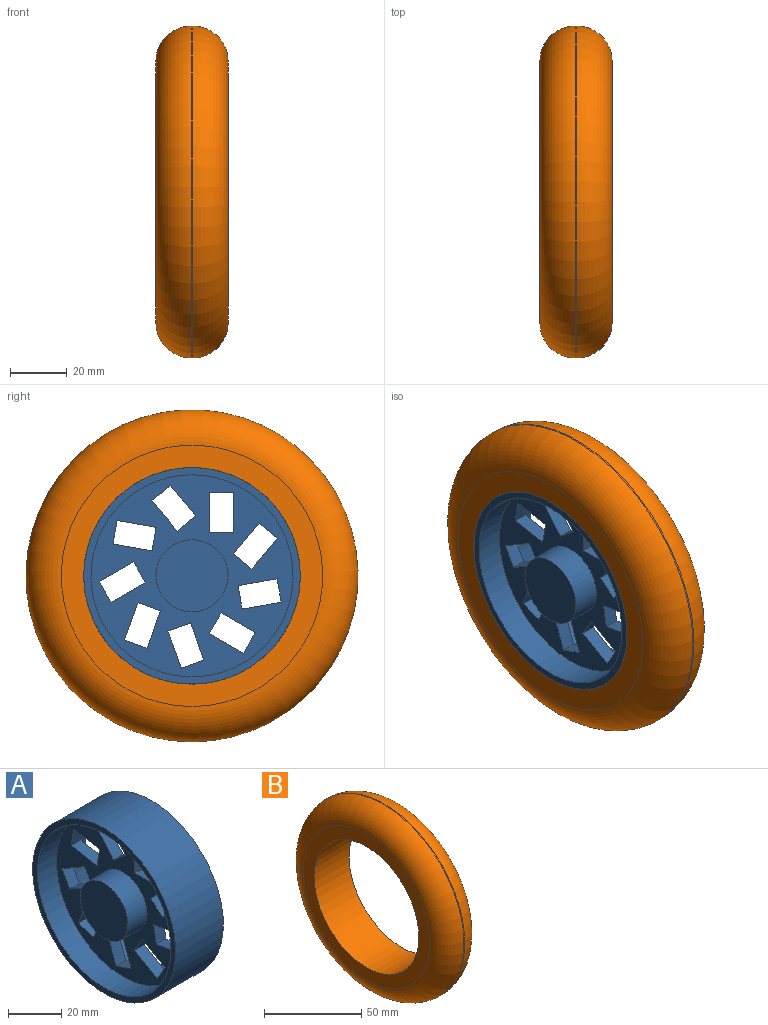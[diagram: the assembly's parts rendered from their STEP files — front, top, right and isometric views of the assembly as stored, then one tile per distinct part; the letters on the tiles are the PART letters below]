
ASSEMBLY  parts=2 mates=1
PART A: 47 faces, bbox 25.4x76.2x76.2 mm
  f0: plane 71.12x71.12mm, normal (1,0,0), area 2410.9mm2, adj f8,f9,f11,f12,f13,f14,f15,f16
  f1: plane 25.4x25.4mm, normal (-1,0,0), area 506.7mm2, adj f2
  f2: cylinder r=12.7mm len=25.4mm, axis (-1,0,0), area 810.7mm2, adj f1,f3
  f3: plane 71.12x71.12mm, normal (-1,0,0), area 2410.9mm2, adj f2,f4,f11,f12,f13,f14,f15,f16
  f4: cylinder r=35.56mm len=71.12mm, axis (-1,0,0), area 2270mm2, adj f3,f5
  f5: plane 76.2x76.2mm, normal (-1,0,0), area 587.8mm2, adj f4,f6
  f6: cylinder r=38.1mm len=76.2mm, axis (-1,0,0), area 6080.5mm2, adj f5,f7
  f7: plane 76.2x76.2mm, normal (1,0,0), area 587.8mm2, adj f6,f8
  f8: cylinder r=35.56mm len=71.12mm, axis (-1,0,0), area 2270mm2, adj f0,f7
  f9: cylinder r=12.7mm len=25.4mm, axis (-1,0,0), area 810.7mm2, adj f0,f10
  f10: plane 25.4x25.4mm, normal (1,0,0), area 506.7mm2, adj f9
  f11: plane 13.94x5.08mm, normal (0,-1,0), area 70.8mm2, adj f0,f3,f12,f14
  f12: plane 8.41x5.08mm, normal (0,0,-1), area 42.7mm2, adj f0,f3,f11,f13
  f13: plane 13.94x5.08mm, normal (0,1,0), area 70.8mm2, adj f0,f3,f12,f14
  f14: plane 8.41x5.08mm, normal (0,0,1), area 42.7mm2, adj f0,f3,f11,f13
  f15: plane 10.68x8.96mm, normal (0,-0.77,0.64), area 70.8mm2, adj f0,f3,f16,f18
  f16: plane 6.44x5.41mm, normal (0,-0.64,-0.77), area 42.7mm2, adj f0,f3,f15,f17
  f17: plane 10.68x8.96mm, normal (0,0.77,-0.64), area 70.8mm2, adj f0,f3,f16,f18
  f18: plane 6.44x5.41mm, normal (0,0.64,0.77), area 42.7mm2, adj f0,f3,f15,f17
  f19: plane 13.72x5.08mm, normal (0,-0.17,0.98), area 70.8mm2, adj f0,f3,f20,f22
  f20: plane 8.28x5.08mm, normal (0,-0.98,-0.17), area 42.7mm2, adj f0,f3,f19,f21
  f21: plane 13.72x5.08mm, normal (0,0.17,-0.98), area 70.8mm2, adj f0,f3,f20,f22
  f22: plane 8.28x5.08mm, normal (0,0.98,0.17), area 42.7mm2, adj f0,f3,f19,f21
  f23: plane 12.07x6.97mm, normal (0,0.5,0.87), area 70.8mm2, adj f0,f3,f24,f26
  f24: plane 7.28x5.08mm, normal (0,-0.87,0.5), area 42.7mm2, adj f0,f3,f23,f25
  f25: plane 12.07x6.97mm, normal (0,-0.5,-0.87), area 70.8mm2, adj f0,f3,f24,f26
  f26: plane 7.28x5.08mm, normal (0,0.87,-0.5), area 42.7mm2, adj f0,f3,f23,f25
  f27: plane 13.1x5.08mm, normal (0,0.94,0.34), area 70.8mm2, adj f0,f3,f28,f30
  f28: plane 7.9x5.08mm, normal (0,-0.34,0.94), area 42.7mm2, adj f0,f3,f27,f29
  f29: plane 13.1x5.08mm, normal (0,-0.94,-0.34), area 70.8mm2, adj f0,f3,f28,f30
  f30: plane 7.9x5.08mm, normal (0,0.34,-0.94), area 42.7mm2, adj f0,f3,f27,f29
  f31: plane 13.1x5.08mm, normal (0,0.94,-0.34), area 70.8mm2, adj f0,f3,f32,f34
  f32: plane 7.9x5.08mm, normal (0,0.34,0.94), area 42.7mm2, adj f0,f3,f31,f33
  f33: plane 13.1x5.08mm, normal (0,-0.94,0.34), area 70.8mm2, adj f0,f3,f32,f34
  f34: plane 7.9x5.08mm, normal (0,-0.34,-0.94), area 42.7mm2, adj f0,f3,f31,f33
  f35: plane 12.07x6.97mm, normal (0,0.5,-0.87), area 70.8mm2, adj f0,f3,f36,f38
  f36: plane 7.28x5.08mm, normal (0,0.87,0.5), area 42.7mm2, adj f0,f3,f35,f37
  f37: plane 12.07x6.97mm, normal (0,-0.5,0.87), area 70.8mm2, adj f0,f3,f36,f38
  f38: plane 7.28x5.08mm, normal (0,-0.87,-0.5), area 42.7mm2, adj f0,f3,f35,f37
  f39: plane 13.72x5.08mm, normal (0,-0.17,-0.98), area 70.8mm2, adj f0,f3,f40,f42
  f40: plane 8.28x5.08mm, normal (0,0.98,-0.17), area 42.7mm2, adj f0,f3,f39,f41
  f41: plane 13.72x5.08mm, normal (0,0.17,0.98), area 70.8mm2, adj f0,f3,f40,f42
  f42: plane 8.28x5.08mm, normal (0,-0.98,0.17), area 42.7mm2, adj f0,f3,f39,f41
  f43: plane 10.68x8.96mm, normal (0,-0.77,-0.64), area 70.8mm2, adj f0,f3,f44,f46
  f44: plane 6.44x5.41mm, normal (0,0.64,-0.77), area 42.7mm2, adj f0,f3,f43,f45
  f45: plane 10.68x8.96mm, normal (0,0.77,0.64), area 70.8mm2, adj f0,f3,f44,f46
  f46: plane 6.44x5.41mm, normal (0,-0.64,0.77), area 42.7mm2, adj f0,f3,f43,f45
PART B: 6 faces, bbox 25.4x126.5x126.5 mm
  f0: cylinder r=38.1mm len=76.2mm, axis (-1,0,0), area 6080.5mm2, adj f2,f3
  f1: cylinder r=58.42mm len=116.84mm, axis (-1,0,0), area 186.5mm2, adj f4,f5
  f2: plane 91.95x91.95mm, normal (1,0,0), area 2079.7mm2, adj f0,f5
  f3: plane 91.95x91.95mm, normal (-1,0,0), area 2079.7mm2, adj f0,f4
  f4: torus R=45.97mm, axis (1,0,0), area 6620.6mm2, adj f1,f3
  f5: torus R=45.97mm, axis (1,0,0), area 6620.6mm2, adj f1,f2
PLACE A t=(-12.7,0,0)mm fixed
PLACE B t=(-25.4,0,0)mm
MATE revolute A.f2 <-> B.f0  axis (1,0,0) through (0,0,0)mm
